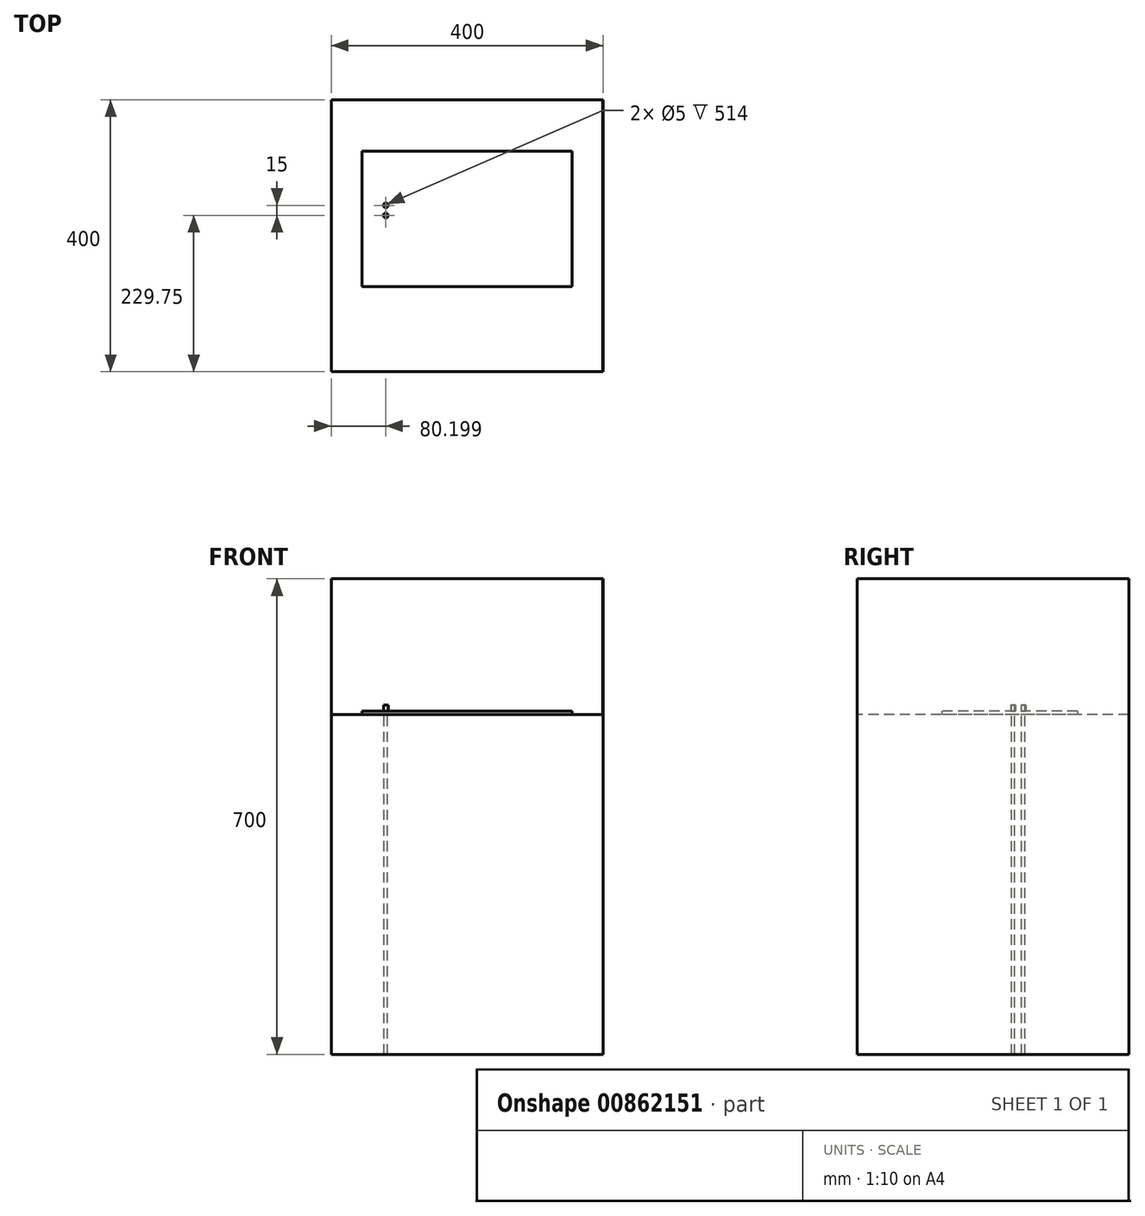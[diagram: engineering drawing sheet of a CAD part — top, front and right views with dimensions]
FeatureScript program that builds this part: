
annotation { "Feature Type Name" : "Feature", "Feature Type Description" : "" }
export const myFeature = defineFeature(function(context is Context, id is Id, definition is map)
    precondition{}
    {
        {
            var Q0;
            Q0=qCreatedBy(makeId("Front.planeOp"),FACE);
            var sketch = newSketch(context, id + "F0", { "sketchPlane" : qUnion([Q0])});
            skLineSegment(sketch, "E0.bottom", {"start": v(0, 0) * mm, "end": v(-400, 0) * mm});
            skLineSegment(sketch, "E0.top", {"start": v(0, 500) * mm, "end": v(-400, 500) * mm});
            skLineSegment(sketch, "E0.left", {"start": v(0, 0) * mm, "end": v(0, 500) * mm});
            skLineSegment(sketch, "E0.right", {"start": v(-400, 0) * mm, "end": v(-400, 500) * mm});
            skSolve(sketch);
        }
        {
            var Q0;
            Q0=makeQuery(id+"F0.imprint","IMPRINT",FACE,{"disambiguationData":[TD([[makeQuery(id+"F0.imprint","IMPRINT",EDGE,{"derivedFrom":sQuery(id+"F0.wireOp",EDGE,"E0.bottom")}),-1.0]])]});
            extrude(context, id + "F1", {"entities" : qUnion([Q0]), "depth" : 400 * mm, "offsetDistance" : 25 * mm});
        }
        {
            var Q0;
            Q0=makeQuery(id+"F1.opExtrude","SWEPT_FACE",FACE,{"disambiguationData":[OSD([sQuery(id+"F0.wireOp",EDGE,"E0.top")])]});
            var sketch = newSketch(context, id + "F2", { "sketchPlane" : qUnion([Q0])});
            skLineSegment(sketch, "E1.bottom", {"start": v(-400, 0) * mm, "end": v(-399.75, 0) * mm});
            skLineSegment(sketch, "E1.top", {"start": v(-400, -400) * mm, "end": v(-399.75, -400) * mm});
            skLineSegment(sketch, "E1.left", {"start": v(-400, 0) * mm, "end": v(-400, -400) * mm});
            skLineSegment(sketch, "E1.right", {"start": v(-399.75, -0.25) * mm, "end": v(-399.75, -400) * mm});
            skLineSegment(sketch, "E2.bottom", {"start": v(-400, 0) * mm, "end": v(0, 0) * mm});
            skLineSegment(sketch, "E2.top", {"start": v(-399.75, -0.25) * mm, "end": v(-0.25, -0.25) * mm});
            skLineSegment(sketch, "E2.left", {"start": v(-400, 0) * mm, "end": v(-400, -0.25) * mm});
            skLineSegment(sketch, "E2.right", {"start": v(0, 0) * mm, "end": v(0, -0.25) * mm});
            skLineSegment(sketch, "E3.bottom", {"start": v(0, -400) * mm, "end": v(-0.25, -400) * mm});
            skLineSegment(sketch, "E3.top", {"start": v(0, 0) * mm, "end": v(-0.25, 0) * mm});
            skLineSegment(sketch, "E3.left", {"start": v(0, -400) * mm, "end": v(0, 0) * mm});
            skLineSegment(sketch, "E3.right", {"start": v(-0.25, -400) * mm, "end": v(-0.25, -0.25) * mm});
            skSolve(sketch);
        }
        {
            var Q0;
            Q0 = qSketchRegion(id + "F2", true);
            extrude(context, id + "F3", {"entities" : qUnion([Q0]), "operationType" : NewBodyOperationType.ADD, "depth" : 200 * mm, "offsetDistance" : 25 * mm});
        }
        {
            var Q0;
            Q0=makeQuery(id+"F1.opExtrude","SWEPT_FACE",FACE,{"disambiguationData":[OSD([sQuery(id+"F0.wireOp",EDGE,"E0.top")])]});
            var sketch = newSketch(context, id + "F4", { "sketchPlane" : qUnion([Q0])});
            skLineSegment(sketch, "E4.bottom", {"start": v(-354.75, -75.25) * mm, "end": v(-45.25, -75.25) * mm});
            skLineSegment(sketch, "E4.top", {"start": v(-354.75, -275.25) * mm, "end": v(-45.25, -275.25) * mm});
            skLineSegment(sketch, "E4.left", {"start": v(-354.75, -75.25) * mm, "end": v(-354.75, -275.25) * mm});
            skLineSegment(sketch, "E4.right", {"start": v(-45.25, -75.25) * mm, "end": v(-45.25, -275.25) * mm});
            skSolve(sketch);
        }
        {
            var Q0;
            Q0 = qSketchRegion(id + "F4", true);
            extrude(context, id + "F5", {"entities" : qUnion([Q0]), "operationType" : NewBodyOperationType.ADD, "depth" : 1 * mm, "offsetDistance" : 25 * mm});
        }
        {
            var Q0;
            Q0 = qSketchRegion(id + "F4", true);
            extrude(context, id + "F6", {"entities" : qUnion([Q0]), "operationType" : NewBodyOperationType.ADD, "depth" : 5 * mm, "offsetDistance" : 25 * mm});
        }
        {
            var Q0;
            Q0=makeQuery(id+"F6.opExtrude","CAP_FACE",FACE,{"disambiguationData":[OSD([sQuery(id+"F4.wireOp",EDGE,"E4.bottom"),sQuery(id+"F4.wireOp",EDGE,"E4.top"),sQuery(id+"F4.wireOp",EDGE,"E4.left"),sQuery(id+"F4.wireOp",EDGE,"E4.right")])],"isStart":false});
            var sketch = newSketch(context, id + "F7", { "sketchPlane" : qUnion([Q0])});
            skSolve(sketch);
        }
        {
            var Q0;
            Q0=makeQuery(id+"F7.imprint","IMPRINT",FACE,{"disambiguationData":[TD([[makeQuery(id+"F7.imprint","IMPRINT",EDGE,{"derivedFrom":makeQuery(id+"F6.opExtrude","CAP_EDGE",EDGE,{"disambiguationData":[OSD([sQuery(id+"F4.wireOp",EDGE,"E4.bottom")])],"isStart":false})}),-1.0]])]});
            var sketch = newSketch(context, id + "F8", { "sketchPlane" : qUnion([Q0])});
            skCircle(sketch, "E5", {"center": v(-319.8, -155.25) * mm, "radius": 3.5 * mm});
            skCircle(sketch, "E6", {"center": v(-319.8, -170.25) * mm, "radius": 3.5 * mm});
            skSolve(sketch);
        }
        {
            var Q0;
            Q0 = qSketchRegion(id + "F8", true);
            extrude(context, id + "F9", {"entities" : qUnion([Q0]), "operationType" : NewBodyOperationType.ADD, "depth" : 9 * mm, "offsetDistance" : 25 * mm});
        }
        {
            var Q0;
            Q0=makeQuery(id+"F9.opExtrude","CAP_FACE",FACE,{"disambiguationData":[OSD([sQuery(id+"F8.wireOp",EDGE,"E5")])],"isStart":false});
            var sketch = newSketch(context, id + "F10", { "sketchPlane" : qUnion([Q0])});
            skCircle(sketch, "E7", {"center": v(-319.8, -155.25) * mm, "radius": 2.95 * mm});
            skSolve(sketch);
        }
        {
            var Q0;
            Q0=sQuery(id+"F10.wireOp",VERTEX,"E7.center");
            var Q1;
            Q1=makeQuery(id+"F1.opExtrude","SWEPT_BODY",BODY,{"disambiguationData":[OSD([sQuery(id+"F0.wireOp",EDGE,"E0.bottom"),sQuery(id+"F0.wireOp",EDGE,"E0.top"),sQuery(id+"F0.wireOp",EDGE,"E0.left"),sQuery(id+"F0.wireOp",EDGE,"E0.right")])]});
            hole(context, id + "F11", {"style" : HoleStyle.SIMPLE, "endStyle" : HoleEndStyle.THROUGH, "holeDiameter" : 5 * mm, "majorDiameter" : 5 * mm, "isTappedThrough" : true, "tappedDepth" : 12 * mm, "tapClearance" : 3, "locations" : qUnion([Q0]), "scope" : qUnion([Q1])});
        }
        {
            var Q0;
            Q0=makeQuery(id+"F9.opExtrude","CAP_FACE",FACE,{"disambiguationData":[OSD([sQuery(id+"F8.wireOp",EDGE,"E6")])],"isStart":false});
            var sketch = newSketch(context, id + "F12", { "sketchPlane" : qUnion([Q0])});
            skCircle(sketch, "E8", {"center": v(-319.8, -170.25) * mm, "radius": 2.45 * mm});
            skSolve(sketch);
        }
        {
            var Q0;
            Q0=sQuery(id+"F12.wireOp",VERTEX,"E8.center");
            var Q1;
            Q1=makeQuery(id+"F1.opExtrude","SWEPT_BODY",BODY,{"disambiguationData":[OSD([sQuery(id+"F0.wireOp",EDGE,"E0.bottom"),sQuery(id+"F0.wireOp",EDGE,"E0.top"),sQuery(id+"F0.wireOp",EDGE,"E0.left"),sQuery(id+"F0.wireOp",EDGE,"E0.right")])]});
            hole(context, id + "F13", {"style" : HoleStyle.SIMPLE, "endStyle" : HoleEndStyle.THROUGH, "holeDiameter" : 5 * mm, "majorDiameter" : 5 * mm, "isTappedThrough" : true, "tappedDepth" : 12 * mm, "tapClearance" : 3, "locations" : qUnion([Q0]), "scope" : qUnion([Q1])});
        }
    });
